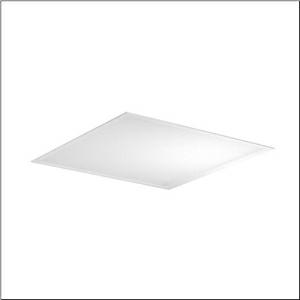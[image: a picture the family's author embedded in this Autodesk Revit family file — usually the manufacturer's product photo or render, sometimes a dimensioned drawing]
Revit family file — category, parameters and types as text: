
# Revit family: apollon_21_square_51mq12wd2453
name_source: partatom
category: Lighting Fixtures
units: mm (PartAtom-declared; Revit-internal decimal feet)

## family parameters
Cut with Voids When Loaded = No
Host = Face
Light Source = No
Part Type = Normal
Room Calculation Point = No
Round Connector Dimension = Use Diameter
Shared = No

## types (1)
- Apollon 21 square (1 x LED, 4000 lm, 33 W, 4000K)
    Apparent Load = 33 VA
    CIE Flux Codes = 62 88 98 100 100
    Color Rendering = 80
    Color Temperature = 4000K
    Default Elevation = 1800 mm
    Description = Apollon 21 square, office luminaire, primary optical cover: micro prismatic cover, of PMMA, CAT 2 (L<= 3000cd/m²), light emission: direct distribution, primary light characteristic: symmetric, installation type: lay-in mounting, recessed, LED, rated luminous flux: 4.000lm, luminous efficacy: 121lm/W, light colour: 840, colour temperature: 4000K, control gear: DALI 2, with terminal, 5-pole, mains connection: 220..240V, AC, 50/60Hz, rated input power: 33W, housing, of aluminium, traffic white (RAL 9016), module: M600, length: 596mm, width: 596mm, height: 40mm, housing upper side, of sheet steel, galvanised, protection rating (complete): IP20, protection rating (lamp compartment, on room side): IP54, insulation class (complete): insulation class II (safety insulation), certification: CE, ENEC, permissible operating ambient temperature: -20..+40°C, packaging unit: 1 piece
    Height = 0 mm  [stored 0 ft]
    Lamp = 1 x LED
    Lamp Light Flux = 4000 lm
    Lamp Power = 33 W
    Lamp count = 1
    Length = 595 mm
    Luminous efficacy = 121 lm/W
    Manufacturer = Siteco
    ModVariant = No
    Model = 51MQ12WD2453
    Mounting Place = Ceiling
    Mounting Type = Recessed
    Number of Poles = 1
    OnlyDefault = Yes
    Power Factor = 1
    Product Name = Apollon 21 square
    Product group = office luminaire | ceiling recessed
    ProductGroupID = 400
    Protection Class = Protection class II
    Protection Degree = IP 20
    RLX_Detail_Level = 1
    RLX_Emergency_Light_Flux = 0 lm
    RLX_Emergency_Type = 0
    RLX_Emergency_Type_DB = No
    RlxData = <blob elided: 12429 chars, md5=877cb058>
    Socket = socket
    Standby Power = 0 W
    System Light Flux = 4000 lm
    System Power = 33 W
    Type Comments = Product without accessories
    Type Image = l_1291049.jpg
    URL = http://relux.com
    VarID = ---
    Voltage = 0 V
    Weight = 0.00 kg
    Width = 595 mm

note: [stored X ft] marks values corroborated as IEEE doubles in the binary element streams (Revit-internal decimal feet)

## geometry (parser evidence)
native form markers: Sweep x10
no freeform markers — native parametric forms only
